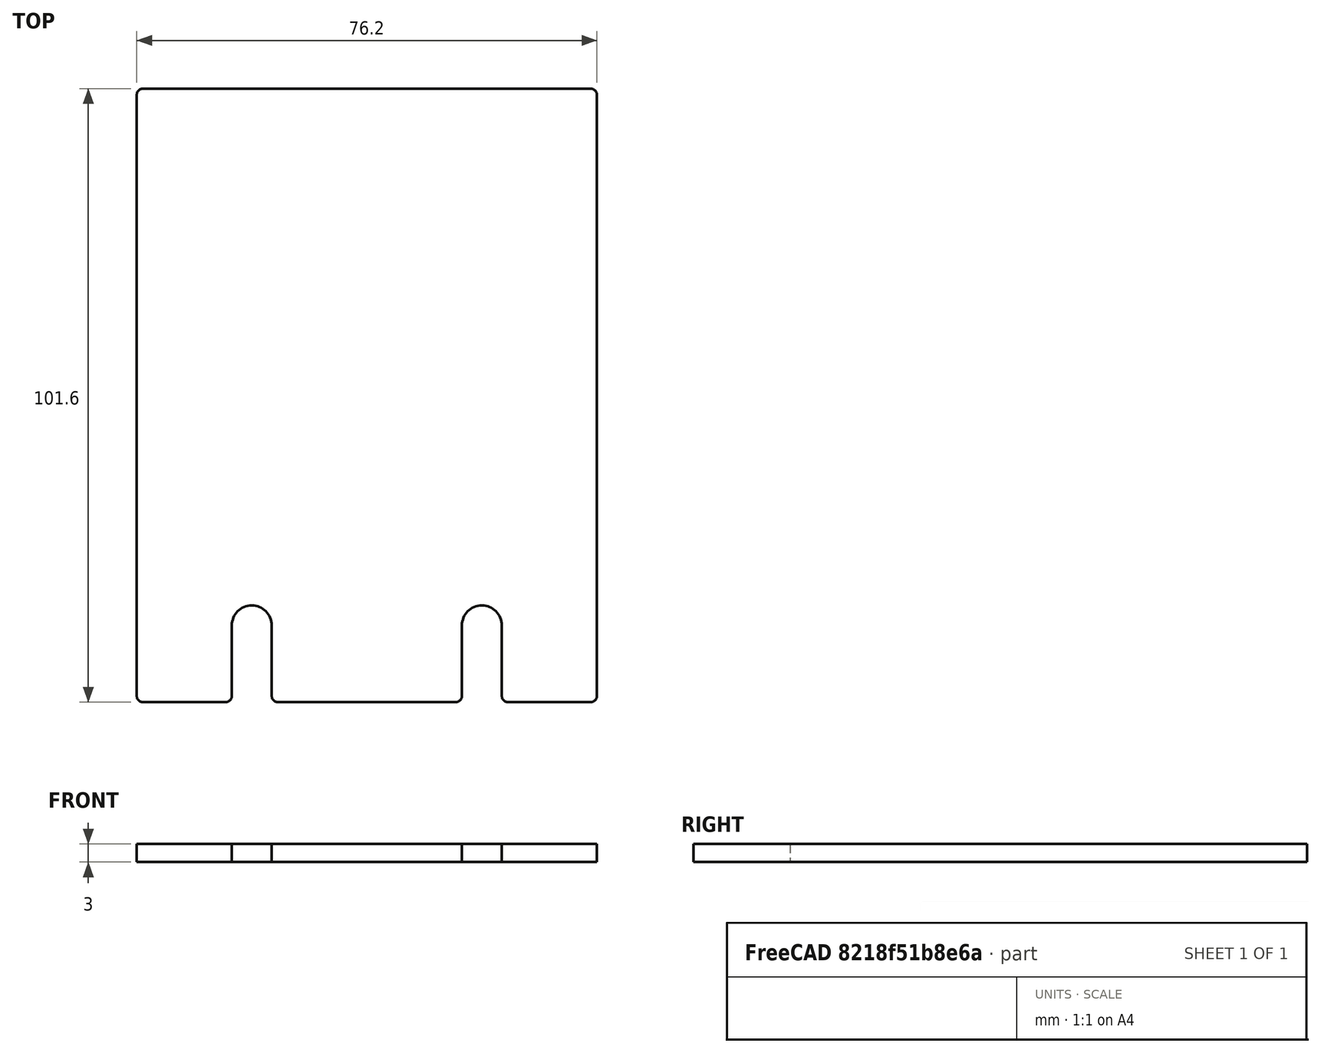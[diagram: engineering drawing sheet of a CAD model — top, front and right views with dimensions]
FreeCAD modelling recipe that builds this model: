
FCSTD DOCUMENT  (FreeCAD 0.21R33675 (Git))
Label: plain_wall_3in
License: All rights reserved
LicenseURL: http://en.wikipedia.org/wiki/All_rights_reserved
objects: Sketcher::SketchObject×1, Spreadsheet::Sheet×1, PartDesign::Pad×1, PartDesign::Body×1
note: 4 computed .brp shape members not serialized (recipe doc carries the construction recipe); baked Part::Feature solids carry a one-line shape summary decoded from their .brp

FEATURE [Sketcher::SketchObject] Sketch
  FullyConstrained = true
  MapMode = 5
  Support = -> [XY_Plane]
  expr: Constraints[19] = Spreadsheet.FilletRadius
  expr: Constraints[21] = Spreadsheet.Height
  expr: Constraints[22] = Spreadsheet.Length
  expr: Constraints[27] = Spreadsheet.MountHoleDistanceFromBottom
  expr: Constraints[29] = Spreadsheet.MountHoleDiameter
  expr: Constraints[35] = Spreadsheet.MountHoleDistanceFromBottom
  expr: Constraints[43] = Spreadsheet.MountHoleSideMargin
  sketch-geometry (30):
    g0: ArcOfCircle CenterX=-37.1 CenterY=49.8 CenterZ=0 NormalX=0 NormalY=0 NormalZ=1 AngleXU=0 Radius=1 StartAngle=1.5708 EndAngle=3.14159
    g1: LineSegment StartX=-37.1 StartY=50.8 StartZ=0 EndX=37.1 EndY=50.8 EndZ=0
    g2: ArcOfCircle CenterX=37.1 CenterY=49.8 CenterZ=0 NormalX=0 NormalY=0 NormalZ=1 AngleXU=0 Radius=1 StartAngle=-1.8e-15 EndAngle=1.5708
    g3: LineSegment StartX=38.1 StartY=49.8 StartZ=0 EndX=38.1 EndY=-49.8 EndZ=0
    g4: ArcOfCircle CenterX=37.1 CenterY=-49.8 CenterZ=0 NormalX=0 NormalY=0 NormalZ=1 AngleXU=0 Radius=1 StartAngle=4.71239 EndAngle=6.28319
    g5: LineSegment StartX=37.1 StartY=-50.8 StartZ=0 EndX=-37.1 EndY=-50.8 EndZ=0
    g6: ArcOfCircle CenterX=-37.1 CenterY=-49.8 CenterZ=0 NormalX=0 NormalY=0 NormalZ=1 AngleXU=0 Radius=1 StartAngle=3.14159 EndAngle=4.71239
    g7: LineSegment StartX=-38.1 StartY=-49.8 StartZ=0 EndX=-38.1 EndY=49.8 EndZ=0
    g8: GeomPoint X=-38.1 Y=50.8 Z=0
    g9: GeomPoint X=38.1 Y=-50.8 Z=0
    g10: LineSegment StartX=-19.05 StartY=-38.1 StartZ=0 EndX=19.05 EndY=-38.1 EndZ=0
    g11: LineSegment StartX=0 StartY=-50.8 StartZ=0 EndX=0 EndY=-38.1 EndZ=0
    g12: Circle CenterX=-19.05 CenterY=-38.1 CenterZ=0 NormalX=0 NormalY=0 NormalZ=1 AngleXU=0 Radius=3.302
    g13: Circle CenterX=19.05 CenterY=-38.1 CenterZ=0 NormalX=0 NormalY=0 NormalZ=1 AngleXU=0 Radius=3.302
    g14: LineSegment StartX=0 StartY=-38.1 StartZ=0 EndX=0 EndY=-50.8 EndZ=0
    g15: LineSegment StartX=-19.05 StartY=-38.1 StartZ=0 EndX=-38.1 EndY=-38.1 EndZ=0
    g16: LineSegment StartX=19.05 StartY=-38.1 StartZ=0 EndX=38.1 EndY=-38.1 EndZ=0
    g17: ArcOfCircle CenterX=-19.05 CenterY=-38.1 CenterZ=0 NormalX=0 NormalY=0 NormalZ=1 AngleXU=0 Radius=3.302 StartAngle=-9e-16 EndAngle=3.14159
    g18: LineSegment StartX=-22.352 StartY=-38.1 StartZ=0 EndX=-22.352 EndY=-49.8 EndZ=0
    g19: LineSegment StartX=-15.748 StartY=-38.1 StartZ=0 EndX=-15.748 EndY=-49.8 EndZ=0
    g20: ArcOfCircle CenterX=-23.352 CenterY=-49.8 CenterZ=0 NormalX=0 NormalY=0 NormalZ=1 AngleXU=0 Radius=1 StartAngle=4.71239 EndAngle=6.28319
    g21: ArcOfCircle CenterX=-14.748 CenterY=-49.8 CenterZ=0 NormalX=0 NormalY=0 NormalZ=1 AngleXU=0 Radius=1 StartAngle=3.14159 EndAngle=4.71239
    g22: ArcOfCircle CenterX=19.05 CenterY=-38.1 CenterZ=0 NormalX=0 NormalY=0 NormalZ=1 AngleXU=0 Radius=3.302 StartAngle=-9e-16 EndAngle=3.14159
    g23: LineSegment StartX=15.748 StartY=-38.1 StartZ=0 EndX=15.748 EndY=-49.8 EndZ=0
    g24: LineSegment StartX=22.352 StartY=-38.1 StartZ=0 EndX=22.352 EndY=-49.8 EndZ=0
    g25: ArcOfCircle CenterX=14.748 CenterY=-49.8 CenterZ=0 NormalX=0 NormalY=0 NormalZ=1 AngleXU=0 Radius=1 StartAngle=4.71239 EndAngle=6.28319
    g26: ArcOfCircle CenterX=23.352 CenterY=-49.8 CenterZ=0 NormalX=0 NormalY=0 NormalZ=1 AngleXU=0 Radius=1 StartAngle=3.14159 EndAngle=4.71239
    g27: LineSegment StartX=-37.1 StartY=-50.8 StartZ=0 EndX=-23.352 EndY=-50.8 EndZ=0
    g28: LineSegment StartX=-14.748 StartY=-50.8 StartZ=0 EndX=14.748 EndY=-50.8 EndZ=0
    g29: LineSegment StartX=23.352 StartY=-50.8 StartZ=0 EndX=37.1 EndY=-50.8 EndZ=0
  constraints (78):
    c: Tangent(g0,g1) = 1.5708
    c: Tangent(g1,g2) = 1.5708
    c: Tangent(g2,g3) = 1.5708
    c: Tangent(g3,g4) = 1.5708
    c: Tangent(g4,g5) = 1.5708
    c: Tangent(g5,g6) = 1.5708
    c: Tangent(g6,g7) = 1.5708
    c: Tangent(g7,g0) = 1.5708
    c: Horizontal(g1)
    c: Horizontal(g5)
    c: Vertical(g3)
    c: Vertical(g7)
    c: Equal(g0,g2)
    c: Equal(g2,g4)
    c: Equal(g4,g6)
    c: PointOnObject(g8,g1)
    c: PointOnObject(g8,g7)
    c: PointOnObject(g9,g3)
    c: PointOnObject(g9,g5)
    c: Radius(g2) = 1
    c: Symmetric(g8,g9,g-1)
    c: DistanceY(g4,g1) = 101.6
    c: DistanceX(g0,g2) = 76.2
    c: Horizontal(g10)
    c: Vertical(g11)
    c: PointOnObject(g11,g5)
    c: PointOnObject(g11,g-2)
    c: DistanceY(g11,g11) = 12.7
    c: Coincident(g13,g10)
    c: Diameter(g13) = 6.604
    c: Equal(g12,g13)
    c: Coincident(g12,g10)
    c: PointOnObject(g14,g10)
    c: Vertical(g14)
    c: Coincident(g14,g11)
    c: DistanceY(g14,g14) = 12.7
    c: Coincident(g15,g12)
    c: PointOnObject(g15,g7)
    c: Horizontal(g15)
    c: Coincident(g16,g13)
    c: PointOnObject(g16,g3)
    c: Horizontal(g16)
    c: Equal(g16,g15)
    c: DistanceX(g15,g15) = 19.05
    c: Coincident(g17,g10)
    c: PointOnObject(g17,g15)
    c: PointOnObject(g17,g10)
    c: PointOnObject(g17,g12)
    c: Coincident(g18,g17)
    c: Vertical(g18)
    c: Coincident(g19,g17)
    c: Vertical(g19)
    c: Equal(g18,g19)
    c: Tangent(g20,g18) = 1.5708
    c: Tangent(g20,g5) = 1.5708
    c: Tangent(g21,g19) = -1.5708
    c: Tangent(g21,g5) = 1.5708
    c: Equal(g20,g6)
    c: Coincident(g22,g10)
    c: PointOnObject(g22,g10)
    c: PointOnObject(g22,g16)
    c: PointOnObject(g22,g13)
    c: Coincident(g23,g22)
    c: Vertical(g23)
    c: Coincident(g24,g22)
    c: Vertical(g24)
    c: Equal(g23,g24)
    c: Tangent(g26,g24) = -1.5708
    c: Tangent(g26,g5) = 1.5708
    c: Tangent(g25,g23) = 1.5708
    c: Tangent(g25,g5) = 1.5708
    c: Equal(g26,g4)
    c: Coincident(g27,g6)
    c: Coincident(g27,g20)
    c: Coincident(g28,g21)
    c: Coincident(g28,g25)
    c: Coincident(g29,g26)
    c: Coincident(g29,g4)
FEATURE [Spreadsheet::Sheet] Spreadsheet
  cells = A2='Parameters; A3='Height; B3(Height)==4 in; A4='Length; B4(Length)==3 in; A5='Thickness; B5(Thickness)==3 mm; A6='FilletRadius; B6(FilletRadius)==1 mm; A7='MountHoleDiameter; B7(MountHoleDiameter)==0.26 in; A8='MountHoleDistanceFromBottom; B8(MountHoleDistanceFromBottom)==0.5 in; A9='MountHoleSideMargin; B9(MountHoleSideMargin)==0.75 in
FEATURE [PartDesign::Pad] Pad
  Direction = (0,0,1)
  Length = 3
  Length2 = 10
  Profile = -> Sketch
  ReferenceAxis = -> Sketch [N_Axis]
  Type = 0
  expr: Length = Spreadsheet.Thickness
FEATURE [PartDesign::Body] Body
  Group = -> [Sketch,Pad]
  Origin = -> Origin
  Tip = -> Pad
